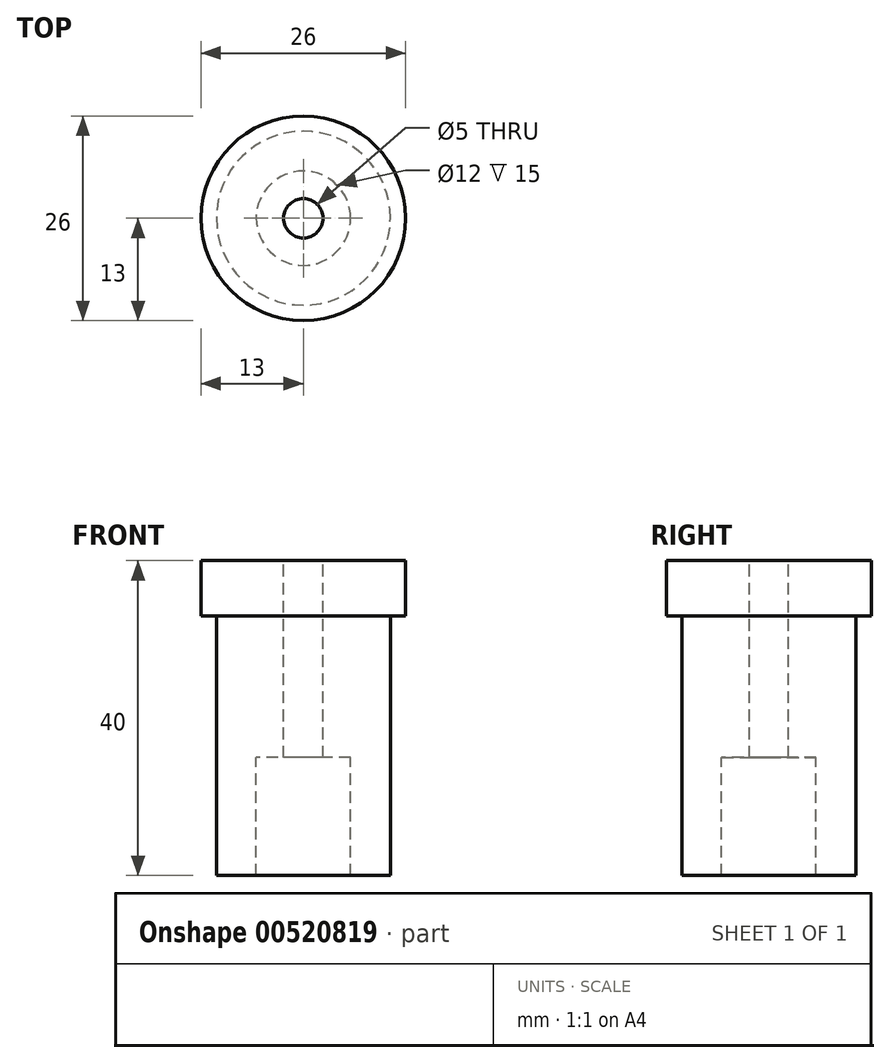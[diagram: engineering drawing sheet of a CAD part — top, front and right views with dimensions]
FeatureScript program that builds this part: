
annotation { "Feature Type Name" : "Feature", "Feature Type Description" : "" }
export const myFeature = defineFeature(function(context is Context, id is Id, definition is map)
    precondition{}
    {
        {
            var Q0;
            Q0=qCreatedBy(makeId("Front.planeOp"),FACE);
            var sketch = newSketch(context, id + "F0", { "sketchPlane" : qUnion([Q0])});
            skLineSegment(sketch, "E0", {"start": v(2.5, 40) * mm, "end": v(2.5, 15) * mm});
            skLineSegment(sketch, "E1", {"start": v(2.5, 40) * mm, "end": v(13, 40) * mm});
            skLineSegment(sketch, "E2", {"start": v(13, 40) * mm, "end": v(13, 33) * mm});
            skLineSegment(sketch, "E3", {"start": v(2.5, 15) * mm, "end": v(6, 15) * mm});
            skLineSegment(sketch, "E4", {"start": v(6, 15) * mm, "end": v(6, 0) * mm});
            skLineSegment(sketch, "E5", {"start": v(13, 33) * mm, "end": v(11.05, 33) * mm});
            skLineSegment(sketch, "E6", {"start": v(11.05, 33) * mm, "end": v(11.05, 0) * mm});
            skLineSegment(sketch, "E7", {"start": v(11.05, 0) * mm, "end": v(6, 0) * mm});
            skLineSegment(sketch, "E8", {"start": v(0, 61.38) * mm, "end": v(0, -7.4) * mm, "construction": true});
            skSolve(sketch);
        }
        {
            var Q0;
            Q0 = qSketchRegion(id + "F0", true);
            var Q1;
            Q1=sQuery(id+"F0.wireOp",EDGE,"E8");
            revolve(context, id + "F1", {"entities" : qUnion([Q0]), "axis" : qUnion([Q1]), "revolveType" : RevolveType.FULL});
        }
    });
